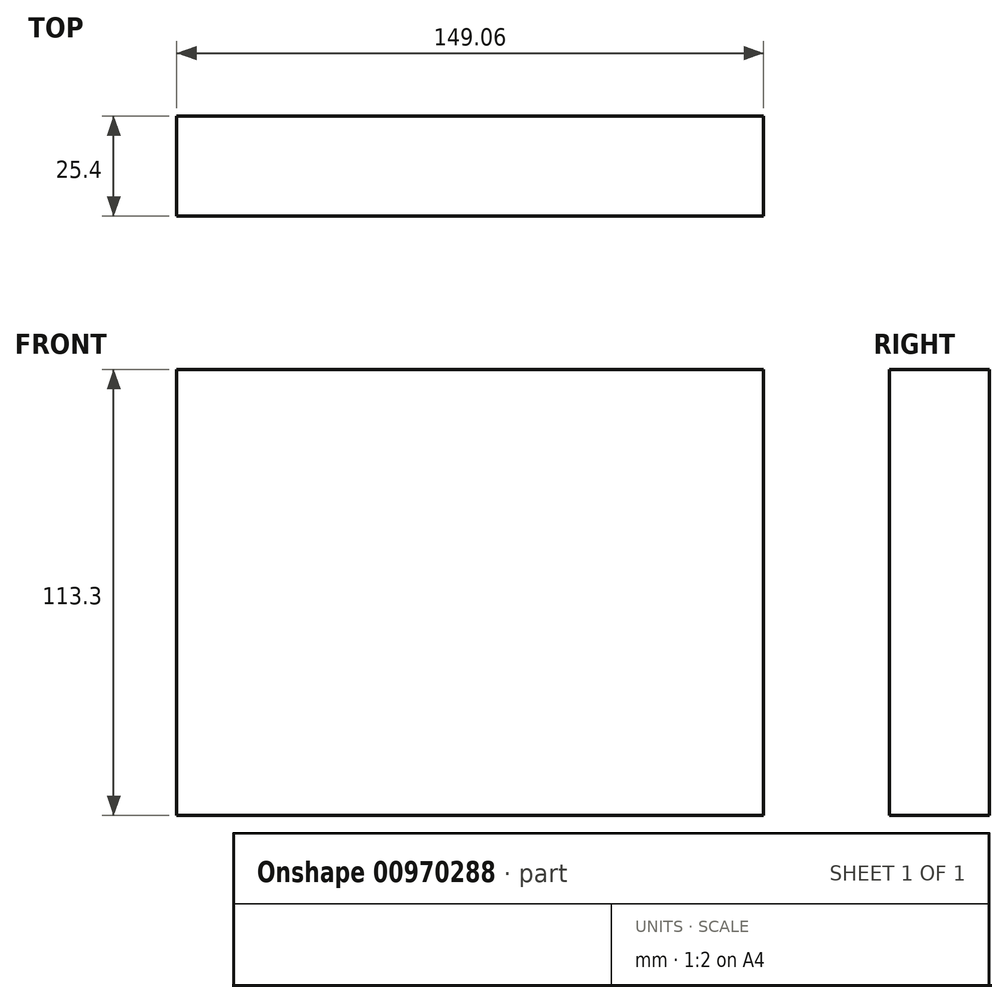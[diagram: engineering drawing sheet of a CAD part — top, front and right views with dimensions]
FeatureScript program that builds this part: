
annotation { "Feature Type Name" : "Feature", "Feature Type Description" : "" }
export const myFeature = defineFeature(function(context is Context, id is Id, definition is map)
    precondition{}
    {
        {
            var Q0;
            Q0=qCreatedBy(makeId("Front.planeOp"),FACE);
            var sketch = newSketch(context, id + "F0", { "sketchPlane" : qUnion([Q0])});
            skLineSegment(sketch, "E0.bottom", {"start": v(74.53, 56.65) * mm, "end": v(-74.53, 56.65) * mm});
            skLineSegment(sketch, "E0.top", {"start": v(74.53, -56.65) * mm, "end": v(-74.53, -56.65) * mm});
            skLineSegment(sketch, "E0.left", {"start": v(74.53, 56.65) * mm, "end": v(74.53, -56.65) * mm});
            skLineSegment(sketch, "E0.right", {"start": v(-74.53, 56.65) * mm, "end": v(-74.53, -56.65) * mm});
            skPoint(sketch, "E0.middle", {"position": v(0, 0) * mm});
            skLineSegment(sketch, "E1.bottom", {"start": v(60.22, 41.25) * mm, "end": v(-60.22, 41.25) * mm});
            skLineSegment(sketch, "E1.top", {"start": v(60.22, -41.25) * mm, "end": v(-60.22, -41.25) * mm});
            skLineSegment(sketch, "E1.left", {"start": v(60.22, 41.25) * mm, "end": v(60.22, -41.25) * mm});
            skLineSegment(sketch, "E1.right", {"start": v(-60.22, 41.25) * mm, "end": v(-60.22, -41.25) * mm});
            skSolve(sketch);
        }
        {
            var Q0;
            Q0=sQuery(id+"F0.wireOp",EDGE,"E0.bottom");
            var Q1;
            Q1=sQuery(id+"F0.wireOp",EDGE,"E0.right");
            var Q2;
            Q2=sQuery(id+"F0.wireOp",EDGE,"E0.top");
            var Q3;
            Q3=sQuery(id+"F0.wireOp",EDGE,"E0.left");
            extrude(context, id + "F1", {"bodyType" : ToolBodyType.SURFACE, "surfaceEntities" : qUnion([Q0, Q1, Q2, Q3]), "depth" : 25.4 * mm, "offsetDistance" : 25.4 * mm});
        }
    });
